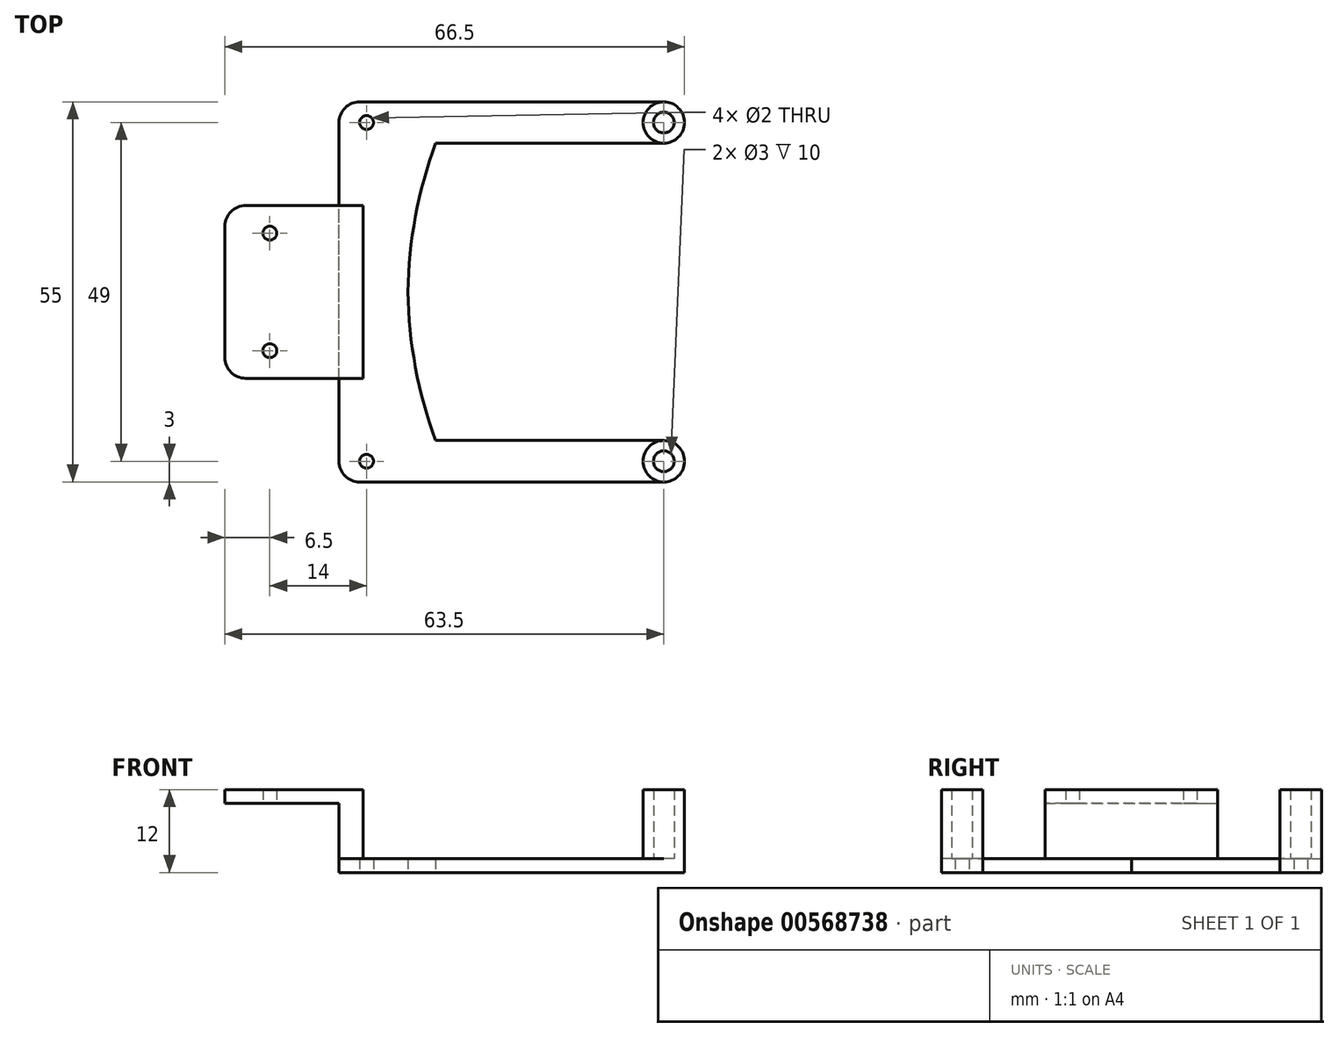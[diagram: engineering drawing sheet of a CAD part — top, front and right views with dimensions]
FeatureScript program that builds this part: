
annotation { "Feature Type Name" : "Feature", "Feature Type Description" : "" }
export const myFeature = defineFeature(function(context is Context, id is Id, definition is map)
    precondition{}
    {
        {
            var Q0;
            Q0=qCreatedBy(makeId("Top.planeOp"),FACE);
            var sketch = newSketch(context, id + "F0", { "sketchPlane" : qUnion([Q0])});
            skLineSegment(sketch, "E0", {"start": v(3, 0) * mm, "end": v(47, 0) * mm});
            skLineSegment(sketch, "E1", {"start": v(50, 3) * mm, "end": v(50, 3) * mm});
            skLineSegment(sketch, "E2", {"start": v(47, 6) * mm, "end": v(14, 6) * mm});
            skLineSegment(sketch, "E3", {"start": v(0, 6) * mm, "end": v(0, 3) * mm});
            skLineSegment(sketch, "E4", {"start": v(0, 6) * mm, "end": v(0, 27.5) * mm});
            skLineSegment(sketch, "E5", {"start": v(0, 27.5) * mm, "end": v(10, 27.5) * mm});
            skPoint(sketch, "E6", {"position": v(10, 27.5) * mm});
            skArc(sketch, "E7", {"start": v(10, 27.5) * mm, "mid": v(11.07, 16.58) * mm, "end": v(14, 6) * mm});
            skPoint(sketch, "E8.visualSharp", {"position": v(0, 0) * mm});
            skArc(sketch, "E8.filletArc", {"start": v(0, 3) * mm, "mid": v(0.88, 0.88) * mm, "end": v(3, 0) * mm});
            skPoint(sketch, "E9.visualSharp", {"position": v(50, 0) * mm});
            skArc(sketch, "E9.filletArc", {"start": v(47, 0) * mm, "mid": v(49.12, 0.88) * mm, "end": v(50, 3) * mm});
            skPoint(sketch, "E10.visualSharp", {"position": v(50, 6) * mm});
            skArc(sketch, "E10.filletArc", {"start": v(50, 3) * mm, "mid": v(49.12, 5.12) * mm, "end": v(47, 6) * mm});
            skCircle(sketch, "E11", {"center": v(4, 3) * mm, "radius": 1 * mm});
            skSolve(sketch);
        }
        {
            var Q0;
            Q0 = qSketchRegion(id + "F0", true);
            extrude(context, id + "F1", {"entities" : qUnion([Q0]), "depth" : 2 * mm, "offsetDistance" : 25 * mm});
        }
        {
            var Q0;
            Q0=makeQuery(id+"F1.opExtrude","CAP_FACE",FACE,{"disambiguationData":[OSD([sQuery(id+"F0.wireOp",EDGE,"E0"),sQuery(id+"F0.wireOp",EDGE,"E2"),sQuery(id+"F0.wireOp",EDGE,"E3"),sQuery(id+"F0.wireOp",EDGE,"E4"),sQuery(id+"F0.wireOp",EDGE,"E5"),sQuery(id+"F0.wireOp",EDGE,"E7"),sQuery(id+"F0.wireOp",EDGE,"E8.filletArc"),sQuery(id+"F0.wireOp",EDGE,"E9.filletArc"),sQuery(id+"F0.wireOp",EDGE,"E10.filletArc")])],"isStart":false});
            var sketch = newSketch(context, id + "F2", { "sketchPlane" : qUnion([Q0])});
            skCircle(sketch, "E12", {"center": v(47, 3) * mm, "radius": 3 * mm});
            skCircle(sketch, "E13", {"center": v(47, 3) * mm, "radius": 1.5 * mm});
            skSolve(sketch);
        }
        {
            var Q0;
            Q0 = qSketchRegion(id + "F2", true);
            extrude(context, id + "F3", {"entities" : qUnion([Q0]), "operationType" : NewBodyOperationType.ADD, "depth" : 10 * mm, "offsetDistance" : 25 * mm});
        }
        {
            var Q0;
            {var subQ0=sQuery(id+"F0.wireOp",EDGE,"E4");var subQ1=sQuery(id+"F0.wireOp",EDGE,"E3");var subQ2=sQuery(id+"F0.wireOp",EDGE,"E2");var subQ3=sQuery(id+"F0.wireOp",EDGE,"E5");var subQ4=sQuery(id+"F0.wireOp",EDGE,"E0");var subQ5=sQuery(id+"F0.wireOp",EDGE,"E7");var subQ6=sQuery(id+"F0.wireOp",EDGE,"E8.filletArc");var subQ7=sQuery(id+"F0.wireOp",EDGE,"E10.filletArc");var subQ8=sQuery(id+"F0.wireOp",EDGE,"E9.filletArc");Q0=makeQuery(id+"F3.boolean.opBoolean","SPLIT",FACE,{"disambiguationData":[TD([makeQuery(id+"F1.opExtrude","SWEPT_FACE",FACE,{"disambiguationData":[OSD([subQ4])]})])],"derivedFrom":makeQuery(id+"F1.opExtrude","CAP_FACE",FACE,{"disambiguationData":[OSD([subQ4,subQ2,subQ1,subQ0,subQ3,subQ5,subQ6,subQ8,subQ7])],"isStart":false})});}
            var sketch = newSketch(context, id + "F4", { "sketchPlane" : qUnion([Q0])});
            skLineSegment(sketch, "E14", {"start": v(0, 27.5) * mm, "end": v(0, 15) * mm});
            skLineSegment(sketch, "E15", {"start": v(0, 15) * mm, "end": v(3.5, 15) * mm});
            skLineSegment(sketch, "E16", {"start": v(3.5, 15) * mm, "end": v(3.5, 27.5) * mm});
            skLineSegment(sketch, "E17", {"start": v(3.5, 27.5) * mm, "end": v(0, 27.5) * mm});
            skSolve(sketch);
        }
        {
            var Q0;
            Q0 = qSketchRegion(id + "F4", true);
            extrude(context, id + "F5", {"entities" : qUnion([Q0]), "operationType" : NewBodyOperationType.ADD, "depth" : 6 * mm, "offsetDistance" : 25 * mm});
        }
        {
            var Q0;
            Q0 = qSketchRegion(id + "F4", true);
            extrude(context, id + "F6", {"entities" : qUnion([Q0]), "operationType" : NewBodyOperationType.ADD, "depth" : 8 * mm, "offsetDistance" : 25 * mm});
        }
        {
            var Q0;
            Q0=makeQuery(id+"F6.opExtrude","CAP_FACE",FACE,{"disambiguationData":[OSD([sQuery(id+"F4.wireOp",EDGE,"E14"),sQuery(id+"F4.wireOp",EDGE,"E15"),sQuery(id+"F4.wireOp",EDGE,"E16"),sQuery(id+"F4.wireOp",EDGE,"E17")])],"isStart":false});
            var sketch = newSketch(context, id + "F7", { "sketchPlane" : qUnion([Q0])});
            skLineSegment(sketch, "E18", {"start": v(3.5, 27.5) * mm, "end": v(-16.5, 27.5) * mm});
            skLineSegment(sketch, "E19", {"start": v(-16.5, 27.5) * mm, "end": v(-16.5, 18) * mm});
            skLineSegment(sketch, "E20", {"start": v(-13.5, 15) * mm, "end": v(3.5, 15) * mm});
            skLineSegment(sketch, "E21", {"start": v(3.5, 15) * mm, "end": v(3.5, 27.5) * mm});
            skCircle(sketch, "E22", {"center": v(-10, 19) * mm, "radius": 1 * mm});
            skPoint(sketch, "E23.visualSharp", {"position": v(-16.5, 15) * mm});
            skArc(sketch, "E23.filletArc", {"start": v(-16.5, 18) * mm, "mid": v(-15.62, 15.88) * mm, "end": v(-13.5, 15) * mm});
            skSolve(sketch);
        }
        {
            var Q0;
            Q0 = qSketchRegion(id + "F7", true);
            extrude(context, id + "F8", {"entities" : qUnion([Q0]), "operationType" : NewBodyOperationType.ADD, "depth" : 2 * mm, "offsetDistance" : 25 * mm});
        }
        {
            var Q0;
            Q0=makeQuery(id+"F1.opExtrude","SWEPT_BODY",BODY,{"disambiguationData":[OSD([sQuery(id+"F0.wireOp",EDGE,"E0"),sQuery(id+"F0.wireOp",EDGE,"E2"),sQuery(id+"F0.wireOp",EDGE,"E3"),sQuery(id+"F0.wireOp",EDGE,"E4"),sQuery(id+"F0.wireOp",EDGE,"E5"),sQuery(id+"F0.wireOp",EDGE,"E7"),sQuery(id+"F0.wireOp",EDGE,"E8.filletArc"),sQuery(id+"F0.wireOp",EDGE,"E9.filletArc"),sQuery(id+"F0.wireOp",EDGE,"E10.filletArc")])]});
            var Q1;
            {var subQ0=sQuery(id+"F4.wireOp",EDGE,"E17");Q1=makeQuery(id+"F8.boolean.opBoolean","MERGE",FACE,{"derivedFrom":[makeQuery(id+"F6.boolean.opBoolean","MERGE",FACE,{"derivedFrom":[makeQuery(id+"F5.boolean.opBoolean","MERGE",FACE,{"derivedFrom":[makeQuery(id+"F1.opExtrude","SWEPT_FACE",FACE,{"disambiguationData":[OSD([sQuery(id+"F0.wireOp",EDGE,"E5")])]}),makeQuery(id+"F5.opExtrude","SWEPT_FACE",FACE,{"disambiguationData":[OSD([subQ0])]})]}),makeQuery(id+"F6.opExtrude","SWEPT_FACE",FACE,{"disambiguationData":[OSD([subQ0])]})]}),makeQuery(id+"F8.opExtrude","SWEPT_FACE",FACE,{"disambiguationData":[OSD([sQuery(id+"F7.wireOp",EDGE,"E18")])]})]});}
            mirror(context, id + "F9", {"operationType" : NewBodyOperationType.ADD, "entities" : qUnion([Q0]), "mirrorPlane" : qUnion([Q1])});
        }
    });
